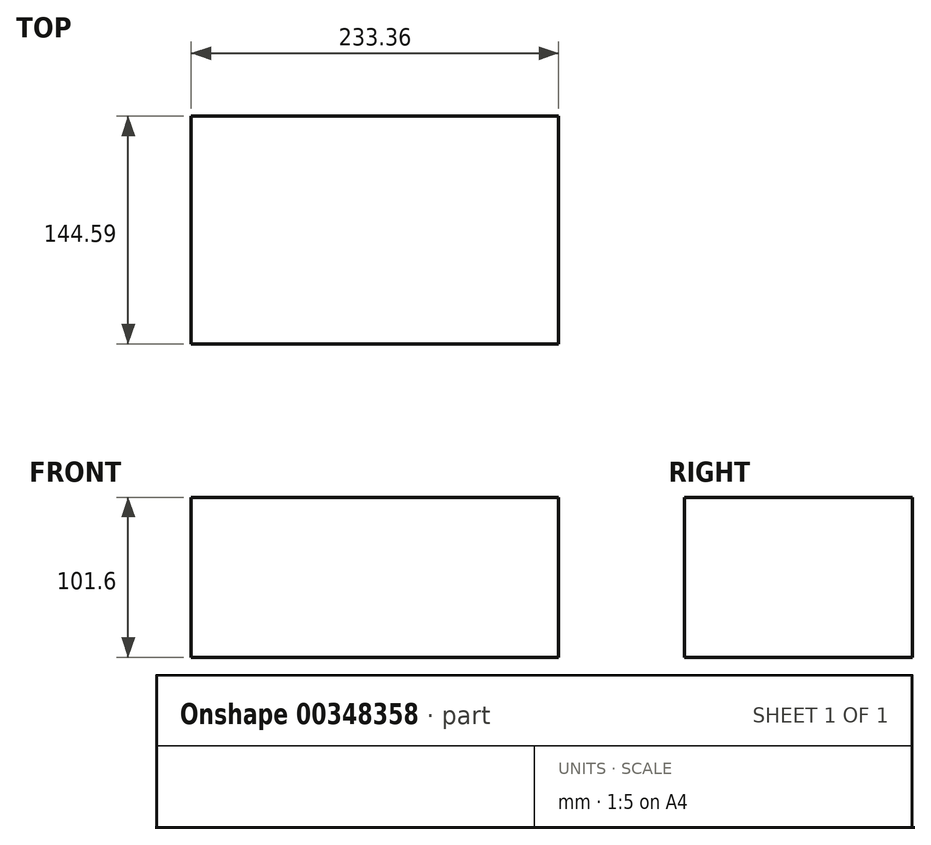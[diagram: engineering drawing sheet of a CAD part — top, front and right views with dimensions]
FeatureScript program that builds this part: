
annotation { "Feature Type Name" : "Feature", "Feature Type Description" : "" }
export const myFeature = defineFeature(function(context is Context, id is Id, definition is map)
    precondition{}
    {
        {
            var Q0;
            Q0=qCreatedBy(makeId("Top.planeOp"),FACE);
            var sketch = newSketch(context, id + "F0", { "sketchPlane" : qUnion([Q0])});
            skLineSegment(sketch, "E0.bottom", {"start": v(-118.03, -31.18) * mm, "end": v(115.33, -31.18) * mm});
            skLineSegment(sketch, "E0.top", {"start": v(-118.03, 113.41) * mm, "end": v(115.33, 113.41) * mm});
            skLineSegment(sketch, "E0.left", {"start": v(-118.03, -31.18) * mm, "end": v(-118.03, 113.41) * mm});
            skLineSegment(sketch, "E0.right", {"start": v(115.33, -31.18) * mm, "end": v(115.33, 113.41) * mm});
            skSolve(sketch);
        }
        {
            var Q0;
            Q0=makeQuery(id+"F0.imprint","IMPRINT",FACE,{"disambiguationData":[TD([[makeQuery(id+"F0.imprint","IMPRINT",EDGE,{"derivedFrom":sQuery(id+"F0.wireOp",EDGE,"E0.bottom")}),1.0]])]});
            extrude(context, id + "F1", {"entities" : qUnion([Q0]), "depth" : 101.6 * mm});
        }
    });
